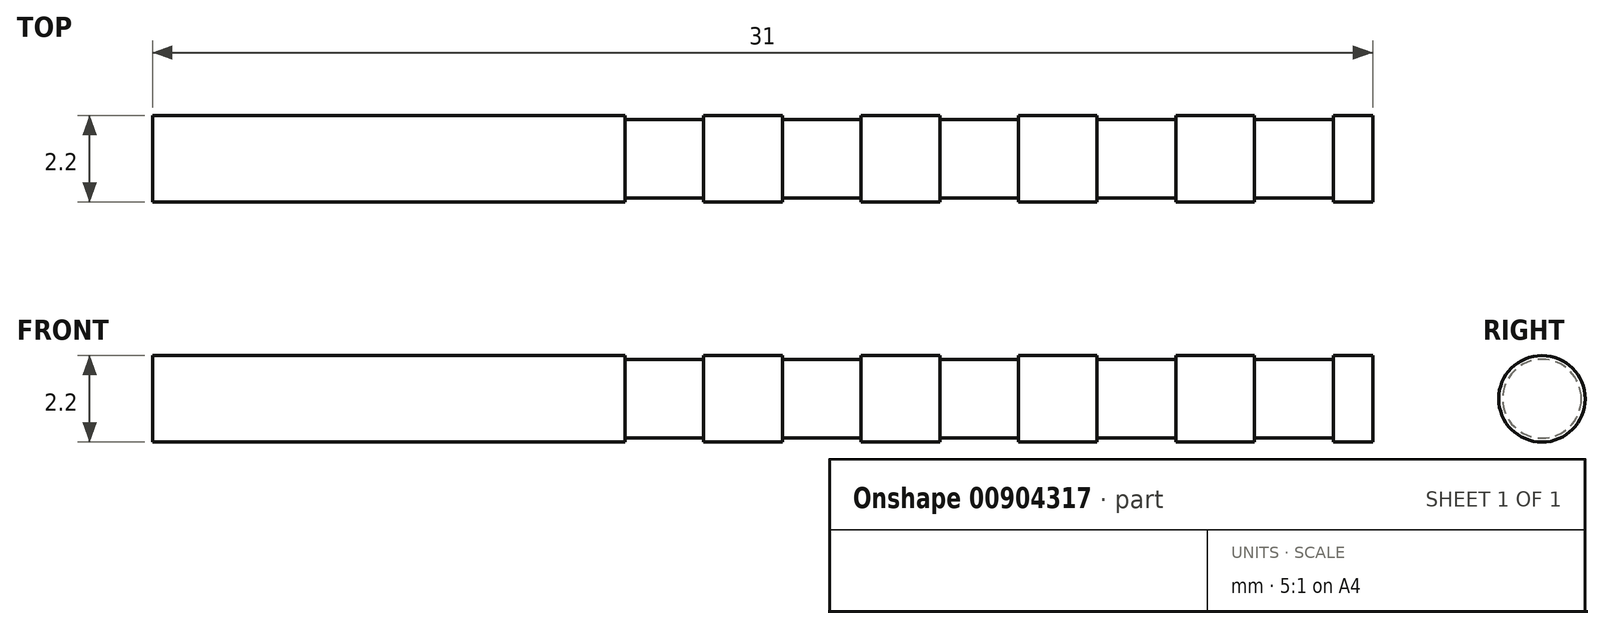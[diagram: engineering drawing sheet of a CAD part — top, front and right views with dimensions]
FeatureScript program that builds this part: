
annotation { "Feature Type Name" : "Feature", "Feature Type Description" : "" }
export const myFeature = defineFeature(function(context is Context, id is Id, definition is map)
    precondition{}
    {
        {
            var Q0;
            Q0=qCreatedBy(makeId("Front.planeOp"),FACE);
            var sketch = newSketch(context, id + "F0", { "sketchPlane" : qUnion([Q0])});
            skLineSegment(sketch, "E0.bottom", {"start": v(0, 0) * mm, "end": v(-25, 0) * mm});
            skLineSegment(sketch, "E0.top", {"start": v(0, 1.1) * mm, "end": v(-25, 1.1) * mm});
            skLineSegment(sketch, "E0.left", {"start": v(0, 0) * mm, "end": v(0, 1.1) * mm});
            skLineSegment(sketch, "E0.right", {"start": v(-25, 0) * mm, "end": v(-25, 1.1) * mm});
            skLineSegment(sketch, "E1.top", {"start": v(0, 1) * mm, "end": v(-25, 1) * mm});
            skLineSegment(sketch, "E1.left", {"start": v(0, 0) * mm, "end": v(0, 1) * mm});
            skLineSegment(sketch, "E1.right", {"start": v(-25, 0) * mm, "end": v(-25, 1) * mm});
            skLineSegment(sketch, "E2", {"start": v(-1, 1.1) * mm, "end": v(-1, 0) * mm});
            skLineSegment(sketch, "E3", {"start": v(-3, 1.1) * mm, "end": v(-3, 0) * mm});
            skLineSegment(sketch, "E4", {"start": v(-5, 1.1) * mm, "end": v(-5, 0) * mm});
            skLineSegment(sketch, "E5", {"start": v(-7, 1.1) * mm, "end": v(-7, 0) * mm});
            skLineSegment(sketch, "E6", {"start": v(-9, 1.1) * mm, "end": v(-9, 0) * mm});
            skLineSegment(sketch, "E7", {"start": v(-11, 1.1) * mm, "end": v(-11, 0) * mm});
            skLineSegment(sketch, "E8", {"start": v(-13, 1.1) * mm, "end": v(-13, 0) * mm});
            skLineSegment(sketch, "E9", {"start": v(-15, 1.1) * mm, "end": v(-15, 0) * mm});
            skLineSegment(sketch, "E10", {"start": v(-17, 1.1) * mm, "end": v(-17, 0) * mm});
            skLineSegment(sketch, "E11", {"start": v(-19, 1.1) * mm, "end": v(-19, 0) * mm});
            skSolve(sketch);
        }
        {
            var Q0;
            {var subQ0=sQuery(id+"F0.wireOp",EDGE,"E0.right");Q0=makeQuery(id+"F0.imprint","IMPRINT",FACE,{"disambiguationData":[TD([[makeQuery(id+"F0.imprint","IMPRINT",EDGE,{"derivedFrom":subQ0}),-1.0]])]});}
            var Q1;
            {var subQ0=sQuery(id+"F0.wireOp",EDGE,"E1.right");Q1=makeQuery(id+"F0.imprint","IMPRINT",FACE,{"disambiguationData":[TD([[makeQuery(id+"F0.imprint","IMPRINT",EDGE,{"derivedFrom":subQ0}),-1.0]])]});}
            var Q2;
            {var subQ0=sQuery(id+"F0.wireOp",EDGE,"E7");var subQ1=sQuery(id+"F0.wireOp",EDGE,"E0.bottom");var subQ2=makeQuery(id+"F0.imprint","INTERSECT",VERTEX,{"derivedFrom":[subQ1,subQ0]});Q2=makeQuery(id+"F0.imprint","IMPRINT",FACE,{"disambiguationData":[TD([[makeQuery(id+"F0.imprint","IMPRINT",EDGE,{"disambiguationData":[TD([[subQ2,-1.0]])],"derivedFrom":subQ1}),-1.0]])]});}
            var Q3;
            {var subQ0=sQuery(id+"F0.wireOp",EDGE,"E7");var subQ1=sQuery(id+"F0.wireOp",EDGE,"E0.top");var subQ2=makeQuery(id+"F0.imprint","INTERSECT",VERTEX,{"derivedFrom":[subQ1,subQ0]});Q3=makeQuery(id+"F0.imprint","IMPRINT",FACE,{"disambiguationData":[TD([[makeQuery(id+"F0.imprint","IMPRINT",EDGE,{"disambiguationData":[TD([[subQ2,-1.0]])],"derivedFrom":subQ1}),1.0]])]});}
            var Q4;
            {var subQ0=sQuery(id+"F0.wireOp",EDGE,"E6");var subQ1=sQuery(id+"F0.wireOp",EDGE,"E0.bottom");var subQ2=makeQuery(id+"F0.imprint","INTERSECT",VERTEX,{"derivedFrom":[subQ1,subQ0]});Q4=makeQuery(id+"F0.imprint","IMPRINT",FACE,{"disambiguationData":[TD([[makeQuery(id+"F0.imprint","IMPRINT",EDGE,{"disambiguationData":[TD([[subQ2,-1.0]])],"derivedFrom":subQ1}),-1.0]])]});}
            var Q5;
            {var subQ0=sQuery(id+"F0.wireOp",EDGE,"E5");var subQ1=sQuery(id+"F0.wireOp",EDGE,"E0.bottom");var subQ2=makeQuery(id+"F0.imprint","INTERSECT",VERTEX,{"derivedFrom":[subQ1,subQ0]});Q5=makeQuery(id+"F0.imprint","IMPRINT",FACE,{"disambiguationData":[TD([[makeQuery(id+"F0.imprint","IMPRINT",EDGE,{"disambiguationData":[TD([[subQ2,-1.0]])],"derivedFrom":subQ1}),-1.0]])]});}
            var Q6;
            {var subQ0=sQuery(id+"F0.wireOp",EDGE,"E5");var subQ1=sQuery(id+"F0.wireOp",EDGE,"E0.top");var subQ2=makeQuery(id+"F0.imprint","INTERSECT",VERTEX,{"derivedFrom":[subQ1,subQ0]});Q6=makeQuery(id+"F0.imprint","IMPRINT",FACE,{"disambiguationData":[TD([[makeQuery(id+"F0.imprint","IMPRINT",EDGE,{"disambiguationData":[TD([[subQ2,-1.0]])],"derivedFrom":subQ1}),1.0]])]});}
            var Q7;
            {var subQ0=sQuery(id+"F0.wireOp",EDGE,"E4");var subQ1=sQuery(id+"F0.wireOp",EDGE,"E0.bottom");var subQ2=makeQuery(id+"F0.imprint","INTERSECT",VERTEX,{"derivedFrom":[subQ1,subQ0]});Q7=makeQuery(id+"F0.imprint","IMPRINT",FACE,{"disambiguationData":[TD([[makeQuery(id+"F0.imprint","IMPRINT",EDGE,{"disambiguationData":[TD([[subQ2,-1.0]])],"derivedFrom":subQ1}),-1.0]])]});}
            var Q8;
            {var subQ0=sQuery(id+"F0.wireOp",EDGE,"E3");var subQ1=sQuery(id+"F0.wireOp",EDGE,"E0.bottom");var subQ2=makeQuery(id+"F0.imprint","INTERSECT",VERTEX,{"derivedFrom":[subQ1,subQ0]});Q8=makeQuery(id+"F0.imprint","IMPRINT",FACE,{"disambiguationData":[TD([[makeQuery(id+"F0.imprint","IMPRINT",EDGE,{"disambiguationData":[TD([[subQ2,-1.0]])],"derivedFrom":subQ1}),-1.0]])]});}
            var Q9;
            {var subQ0=sQuery(id+"F0.wireOp",EDGE,"E3");var subQ1=sQuery(id+"F0.wireOp",EDGE,"E0.top");var subQ2=makeQuery(id+"F0.imprint","INTERSECT",VERTEX,{"derivedFrom":[subQ1,subQ0]});Q9=makeQuery(id+"F0.imprint","IMPRINT",FACE,{"disambiguationData":[TD([[makeQuery(id+"F0.imprint","IMPRINT",EDGE,{"disambiguationData":[TD([[subQ2,-1.0]])],"derivedFrom":subQ1}),1.0]])]});}
            var Q10;
            {var subQ0=sQuery(id+"F0.wireOp",EDGE,"E2");var subQ1=sQuery(id+"F0.wireOp",EDGE,"E0.bottom");var subQ2=makeQuery(id+"F0.imprint","INTERSECT",VERTEX,{"derivedFrom":[subQ1,subQ0]});Q10=makeQuery(id+"F0.imprint","IMPRINT",FACE,{"disambiguationData":[TD([[makeQuery(id+"F0.imprint","IMPRINT",EDGE,{"disambiguationData":[TD([[subQ2,-1.0]])],"derivedFrom":subQ1}),-1.0]])]});}
            var Q11;
            {var subQ0=sQuery(id+"F0.wireOp",EDGE,"E1.left");Q11=makeQuery(id+"F0.imprint","IMPRINT",FACE,{"disambiguationData":[TD([[makeQuery(id+"F0.imprint","IMPRINT",EDGE,{"derivedFrom":subQ0}),1.0]])]});}
            var Q12;
            {var subQ0=sQuery(id+"F0.wireOp",EDGE,"E0.left");Q12=makeQuery(id+"F0.imprint","IMPRINT",FACE,{"disambiguationData":[TD([[makeQuery(id+"F0.imprint","IMPRINT",EDGE,{"derivedFrom":subQ0}),1.0]])]});}
            var Q13;
            {var subQ0=sQuery(id+"F0.wireOp",EDGE,"E8");var subQ1=sQuery(id+"F0.wireOp",EDGE,"E0.bottom");var subQ2=makeQuery(id+"F0.imprint","INTERSECT",VERTEX,{"derivedFrom":[subQ1,subQ0]});Q13=makeQuery(id+"F0.imprint","IMPRINT",FACE,{"disambiguationData":[TD([[makeQuery(id+"F0.imprint","IMPRINT",EDGE,{"disambiguationData":[TD([[subQ2,-1.0]])],"derivedFrom":subQ1}),-1.0]])]});}
            var Q14;
            {var subQ0=sQuery(id+"F0.wireOp",EDGE,"E9");var subQ1=sQuery(id+"F0.wireOp",EDGE,"E0.bottom");var subQ2=makeQuery(id+"F0.imprint","INTERSECT",VERTEX,{"derivedFrom":[subQ1,subQ0]});Q14=makeQuery(id+"F0.imprint","IMPRINT",FACE,{"disambiguationData":[TD([[makeQuery(id+"F0.imprint","IMPRINT",EDGE,{"disambiguationData":[TD([[subQ2,-1.0]])],"derivedFrom":subQ1}),-1.0]])]});}
            var Q15;
            {var subQ0=sQuery(id+"F0.wireOp",EDGE,"E9");var subQ1=sQuery(id+"F0.wireOp",EDGE,"E0.top");var subQ2=makeQuery(id+"F0.imprint","INTERSECT",VERTEX,{"derivedFrom":[subQ1,subQ0]});Q15=makeQuery(id+"F0.imprint","IMPRINT",FACE,{"disambiguationData":[TD([[makeQuery(id+"F0.imprint","IMPRINT",EDGE,{"disambiguationData":[TD([[subQ2,-1.0]])],"derivedFrom":subQ1}),1.0]])]});}
            var Q16;
            {var subQ0=sQuery(id+"F0.wireOp",EDGE,"E10");var subQ1=sQuery(id+"F0.wireOp",EDGE,"E0.bottom");var subQ2=makeQuery(id+"F0.imprint","INTERSECT",VERTEX,{"derivedFrom":[subQ1,subQ0]});Q16=makeQuery(id+"F0.imprint","IMPRINT",FACE,{"disambiguationData":[TD([[makeQuery(id+"F0.imprint","IMPRINT",EDGE,{"disambiguationData":[TD([[subQ2,-1.0]])],"derivedFrom":subQ1}),-1.0]])]});}
            var Q17;
            Q17=sQuery(id+"F0.wireOp",EDGE,"E0.bottom");
            revolve(context, id + "F1", {"surfaceOperationType" : NewSurfaceOperationType.NEW, "entities" : qUnion([Q0, Q1, Q2, Q3, Q4, Q5, Q6, Q7, Q8, Q9, Q10, Q11, Q12, Q13, Q14, Q15, Q16]), "axis" : qUnion([Q17]), "revolveType" : RevolveType.FULL});
        }
        {
            var Q0;
            Q0=makeQuery(id+"F1.opRevolve","SWEPT_FACE",FACE,{"disambiguationData":[OSD([sQuery(id+"F0.wireOp",EDGE,"E0.right"),sQuery(id+"F0.wireOp",EDGE,"E1.right")])]});
            extrude(context, id + "F2", {"entities" : qUnion([Q0]), "operationType" : NewBodyOperationType.ADD, "depth" : 6 * mm, "offsetDistance" : 25 * mm});
        }
    });
